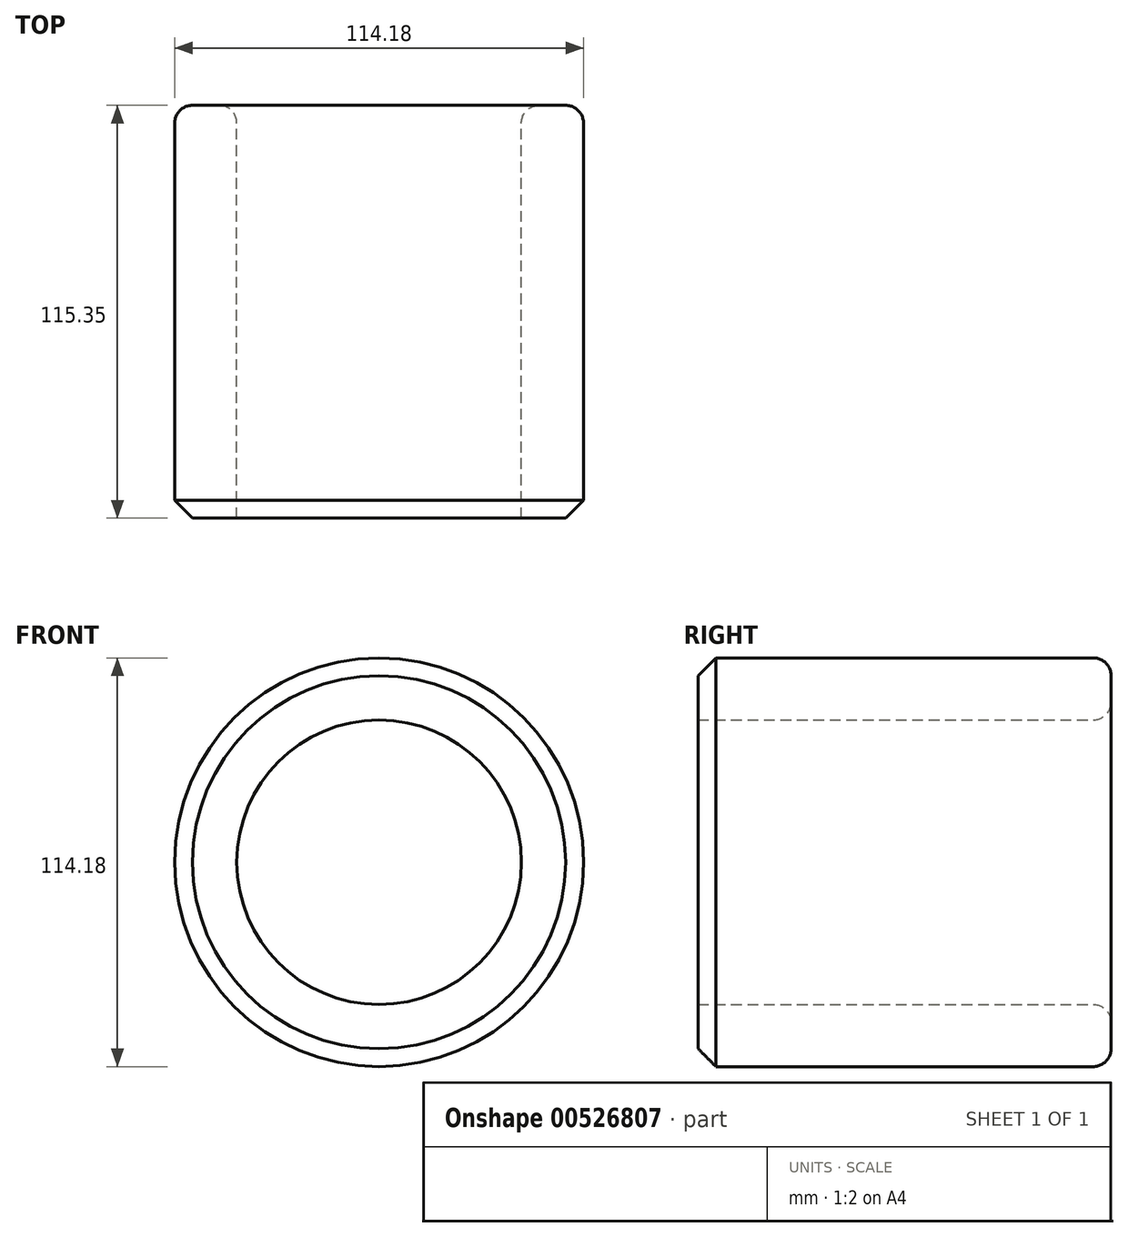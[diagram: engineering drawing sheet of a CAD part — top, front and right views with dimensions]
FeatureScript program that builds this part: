
annotation { "Feature Type Name" : "Feature", "Feature Type Description" : "" }
export const myFeature = defineFeature(function(context is Context, id is Id, definition is map)
    precondition{}
    {
        {
            var Q0;
            Q0=qCreatedBy(makeId("Front.planeOp"),FACE);
            var sketch = newSketch(context, id + "F0", { "sketchPlane" : qUnion([Q0])});
            skCircle(sketch, "E0", {"center": v(0, 0) * mm, "radius": 57.1 * mm});
            skCircle(sketch, "E1", {"center": v(0, 0) * mm, "radius": 39.73 * mm});
            skSolve(sketch);
        }
        {
            var Q0;
            Q0=makeQuery(id+"F0.imprint","IMPRINT",FACE,{"disambiguationData":[TD([[makeQuery(id+"F0.imprint","IMPRINT",EDGE,{"derivedFrom":sQuery(id+"F0.wireOp",EDGE,"E0")}),1.0]])]});
            var Q1;
            Q1=sQuery(id+"F0.wireOp",EDGE,"E1");
            var Q2;
            Q2=sQuery(id+"F0.wireOp",EDGE,"E0");
            extrude(context, id + "F1", {"entities" : qUnion([Q0]), "surfaceEntities" : qUnion([Q1, Q2]), "depth" : 115.35 * mm, "offsetDistance" : 25.4 * mm});
        }
        {
            var Q0;
            Q0=makeQuery(id+"F1.opExtrude","CAP_EDGE",EDGE,{"disambiguationData":[OSD([sQuery(id+"F0.wireOp",EDGE,"E0")])],"isStart":false});
            chamfer(context, id + "F2", {"entities" : qUnion([Q0]), "width" : 5 * mm, "tangentPropagation" : true});
        }
        {
            var Q0;
            Q0=makeQuery(id+"F1.opExtrude","CAP_EDGE",EDGE,{"disambiguationData":[OSD([sQuery(id+"F0.wireOp",EDGE,"E0")])],"isStart":true});
            fillet(context, id + "F3", {"entities" : qUnion([Q0]), "radius" : 5 * mm, "tangentPropagation" : true, "allowEdgeOverflow" : false});
        }
        {
            var Q0;
            Q0=makeQuery(id+"F1.opExtrude","CAP_EDGE",EDGE,{"disambiguationData":[OSD([sQuery(id+"F0.wireOp",EDGE,"E1")])],"isStart":true});
            fillet(context, id + "F4", {"entities" : qUnion([Q0]), "radius" : 5 * mm, "tangentPropagation" : true, "allowEdgeOverflow" : false});
        }
    });
